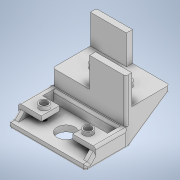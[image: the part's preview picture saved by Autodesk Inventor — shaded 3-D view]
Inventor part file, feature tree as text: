
AUTODESK INVENTOR PART (.ipt)
format: ipt  version: 2020 (Build 240168000, 168)  size: 343,040 bytes
history: native  units: in
note: dims shown in document units (in); Inventor stores cm internally (conversion verified against a paired STEP export)
features: extrude x14, sketch x14, chamfer x2, mirror x1, fillet x1
ambient origin geometry x8: Origin, YZ Plane, XZ Plane, XY Plane, X Axis, Y Axis, Z Axis, Center Point
bodies: Solid1 (feature_tree)
feature tree (32):
  extrude  "Extrusion1"  Depth=1.4331in
  extrude  "Extrusion2"  Depth=1.1811in
  extrude  "Extrusion3"  Depth=1.1811in
  extrude  "Extrusion4"  Depth=0.9606in TaperAngle=0.0deg
  extrude  "Extrusion5"  Depth=0.3406in
  chamfer  "Chamfer1"  Distance=0.1969in
  extrude  "Extrusion6"  Depth=0.1575in
  extrude  "Extrusion7"  Depth=0.2362in
  extrude  "Extrusion8"  Depth=0.1181in TaperAngle=0.0deg
  extrude  "Extrusion9"  Depth=0.0787in
  extrude  "Extrusion10"  Depth=0.1969in
  extrude  "Extrusion11"  Depth=0.8504in TaperAngle=0.0deg
  extrude  "Extrusion12"  Depth=2.5197in
  mirror  "Mirror1"
  extrude  "Extrusion13"  Depth=0.1181in
  chamfer  "Chamfer2"  Distance=0.9311in
  extrude  "Extrusion14"  Depth=0.0787in
  fillet  "Fillet2"  Radius=0.9311in
  sketch  "Sketch1"  dims[d0=2.3937in d1=1.4331in]
  sketch  "Sketch2"  dims[d2=0.1969in d3=0.0in d4=1.1811in]
  sketch  "Sketch3"  dims[d5=0.1969in d6=1.1811in]
  sketch  "Sketch4"  dims[d7=0.1969in d8=0.9606in d9=0.0in]
  sketch  "Sketch5"  dims[d10=0.3406in d11=0.3406in d12=0.1969in d13=0.0in]
  sketch  "Sketch6"  dims[d14=0.1575in d15=0.1575in]
  sketch  "Sketch7"  dims[d16=0.5906in d17=0.0in d18=0.2362in]
  sketch  "Sketch8"  dims[d19=0.2362in d20=0.1181in d21=0.0in]
  sketch  "Sketch9"  dims[d22=0.0591in d23=0.0787in d24=45.0deg d26=0.1969in]
  sketch  "Sketch10"  dims[d27=0.1969in d28=0.1969in]
  sketch  "Sketch11"  dims[d29=0.1969in d30=0.8504in d31=0.0in]
  sketch  "Sketch12"  dims[d32=2.5197in d33=0.1969in]
  sketch  "Sketch13"  dims[d34=1.378in d35=0.0in d36=0.1181in]
  sketch  "Sketch14"  dims[d37=0.1969in d38=0.9311in d39=0.1969in d40=0.9311in d41=0.3543in d42=0.0in d43=0.5906in d44=0.1575in d45=0.5512in d46=0.0in d47=0.315in d48=0.1181in d49=0.0in d50=0.1575in d51=0.7874in d52=0.0in d53=0.2362in d54=0.1181in d55=0.0in d56=0.5906in d57=0.7874in d58=0.0in d59=0.1969in d60=0.0787in d61=45.0deg d62=3.937in d63=0.0in d64=0.0787in]
